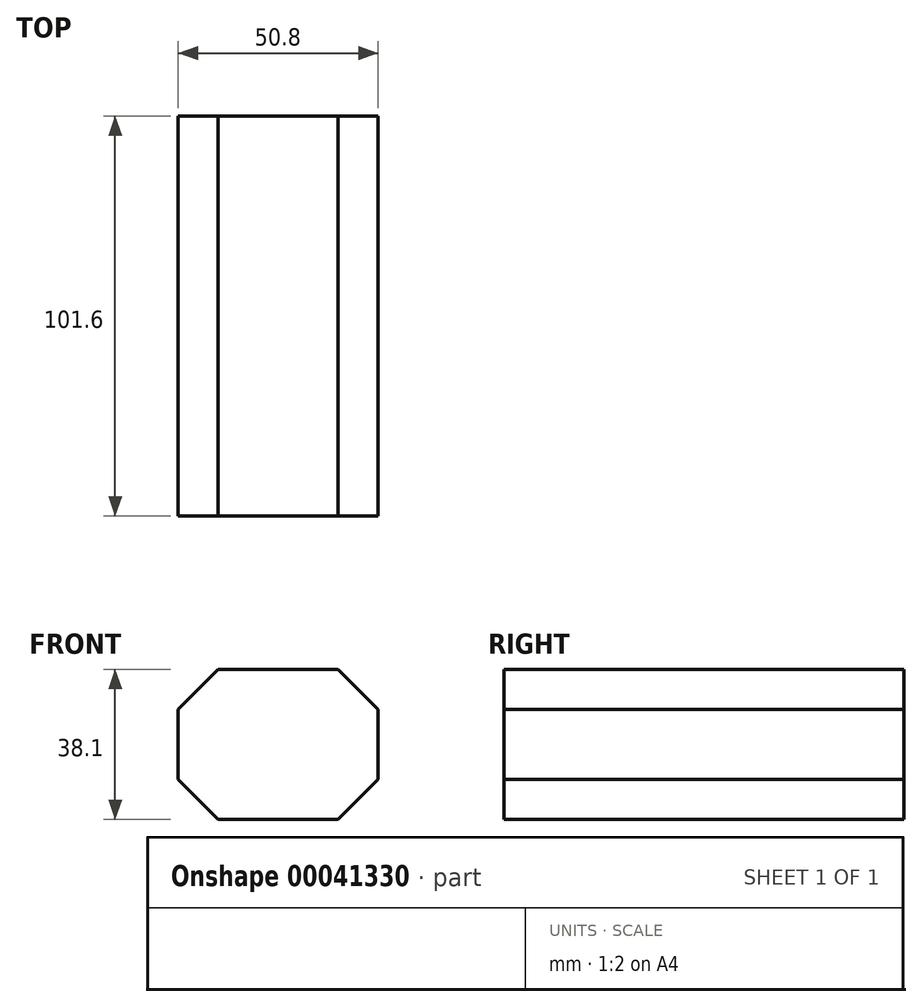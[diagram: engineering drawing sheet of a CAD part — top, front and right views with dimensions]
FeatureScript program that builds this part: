
annotation { "Feature Type Name" : "Feature", "Feature Type Description" : "" }
export const myFeature = defineFeature(function(context is Context, id is Id, definition is map)
    precondition{}
    {
        {
            var Q0;
            Q0=qCreatedBy(makeId("Front.planeOp"),FACE);
            var sketch = newSketch(context, id + "F0", { "sketchPlane" : qUnion([Q0])});
            skLineSegment(sketch, "E0.rect.bottom", {"start": v(-25.4, 19.05) * mm, "end": v(25.4, 19.05) * mm});
            skLineSegment(sketch, "E0.rect.top", {"start": v(-25.4, -19.05) * mm, "end": v(25.4, -19.05) * mm});
            skLineSegment(sketch, "E0.rect.left", {"start": v(-25.4, 19.05) * mm, "end": v(-25.4, -19.05) * mm});
            skLineSegment(sketch, "E0.rect.right", {"start": v(25.4, 19.05) * mm, "end": v(25.4, -19.05) * mm});
            skPoint(sketch, "E0.rect.middle", {"position": v(0, 0) * mm});
            skSolve(sketch);
        }
        {
            var Q0;
            Q0 = qSketchRegion(id + "F0", true);
            extrude(context, id + "F1", {"entities" : qUnion([Q0]), "depth" : 101.6 * mm});
        }
        {
            var Q0;
            Q0=makeQuery(id+"F1.opExtrude","SWEPT_EDGE",EDGE,{"disambiguationData":[OSD([sQuery(id+"F0.wireOp",EDGE,"E0.rect.bottom"),sQuery(id+"F0.wireOp",EDGE,"E0.rect.left")])]});
            var Q1;
            Q1=makeQuery(id+"F1.opExtrude","SWEPT_EDGE",EDGE,{"disambiguationData":[OSD([sQuery(id+"F0.wireOp",EDGE,"E0.rect.top"),sQuery(id+"F0.wireOp",EDGE,"E0.rect.left")])]});
            var Q2;
            Q2=makeQuery(id+"F1.opExtrude","SWEPT_EDGE",EDGE,{"disambiguationData":[OSD([sQuery(id+"F0.wireOp",EDGE,"E0.rect.top"),sQuery(id+"F0.wireOp",EDGE,"E0.rect.right")])]});
            var Q3;
            Q3=makeQuery(id+"F1.opExtrude","SWEPT_EDGE",EDGE,{"disambiguationData":[OSD([sQuery(id+"F0.wireOp",EDGE,"E0.rect.bottom"),sQuery(id+"F0.wireOp",EDGE,"E0.rect.right")])]});
            chamfer(context, id + "F2", {"entities" : qUnion([Q0, Q1, Q2, Q3]), "width" : 10.16 * mm, "tangentPropagation" : true});
        }
    });
